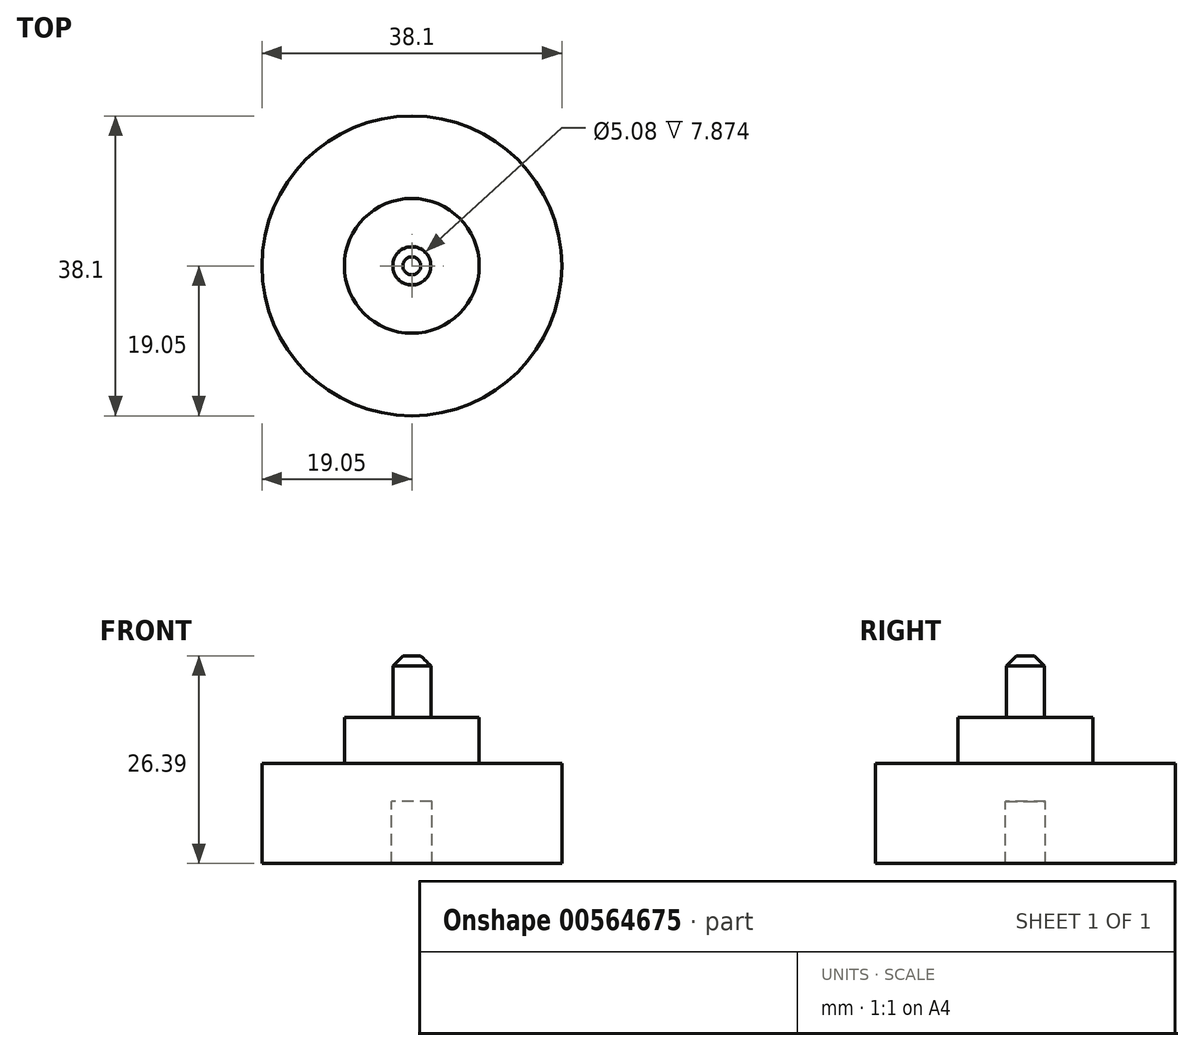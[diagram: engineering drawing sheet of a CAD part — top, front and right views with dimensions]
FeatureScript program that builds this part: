
annotation { "Feature Type Name" : "Feature", "Feature Type Description" : "" }
export const myFeature = defineFeature(function(context is Context, id is Id, definition is map)
    precondition{}
    {
        {
            var Q0;
            Q0=qCreatedBy(makeId("Front.planeOp"),FACE);
            var sketch = newSketch(context, id + "F0", { "sketchPlane" : qUnion([Q0])});
            skLineSegment(sketch, "E0", {"start": v(19.05, 0) * mm, "end": v(19.05, 12.7) * mm});
            skLineSegment(sketch, "E1", {"start": v(19.05, 12.7) * mm, "end": v(8.56, 12.7) * mm});
            skLineSegment(sketch, "E2", {"start": v(2.41, 18.54) * mm, "end": v(8.56, 18.54) * mm});
            skLineSegment(sketch, "E3", {"start": v(8.56, 18.54) * mm, "end": v(8.56, 12.7) * mm});
            skLineSegment(sketch, "E4", {"start": v(0, 26.4) * mm, "end": v(2.41, 26.4) * mm});
            skLineSegment(sketch, "E5", {"start": v(2.41, 26.4) * mm, "end": v(2.41, 18.54) * mm});
            skPoint(sketch, "E5.endSnap0", {"position": v(0, 15.62) * mm});
            skPoint(sketch, "E6.orphan", {"position": v(2.41, 15.62) * mm});
            skLineSegment(sketch, "E7", {"start": v(0, 0) * mm, "end": v(2.54, 0) * mm});
            skLineSegment(sketch, "E8", {"start": v(2.54, 0) * mm, "end": v(2.54, 7.87) * mm});
            skLineSegment(sketch, "E9", {"start": v(2.54, 7.87) * mm, "end": v(0, 7.87) * mm});
            skLineSegment(sketch, "E10", {"start": v(0, 26.4) * mm, "end": v(0, 7.87) * mm});
            skLineSegment(sketch, "E11", {"start": v(2.54, 0) * mm, "end": v(19.05, 0) * mm});
            skSolve(sketch);
        }
        {
            var Q0;
            Q0 = qSketchRegion(id + "F0", true);
            var Q1;
            Q1=sQuery(id+"F0.wireOp",EDGE,"E10");
            revolve(context, id + "F1", {"entities" : qUnion([Q0]), "axis" : qUnion([Q1]), "revolveType" : RevolveType.FULL});
        }
        {
            var Q0;
            Q0=makeQuery(id+"F1.opRevolve","SWEPT_EDGE",EDGE,{"disambiguationData":[OSD([sQuery(id+"F0.wireOp",EDGE,"E4"),sQuery(id+"F0.wireOp",EDGE,"E5")])]});
            chamfer(context, id + "F2", {"entities" : qUnion([Q0]), "width" : 1.27 * mm, "tangentPropagation" : true});
        }
    });
